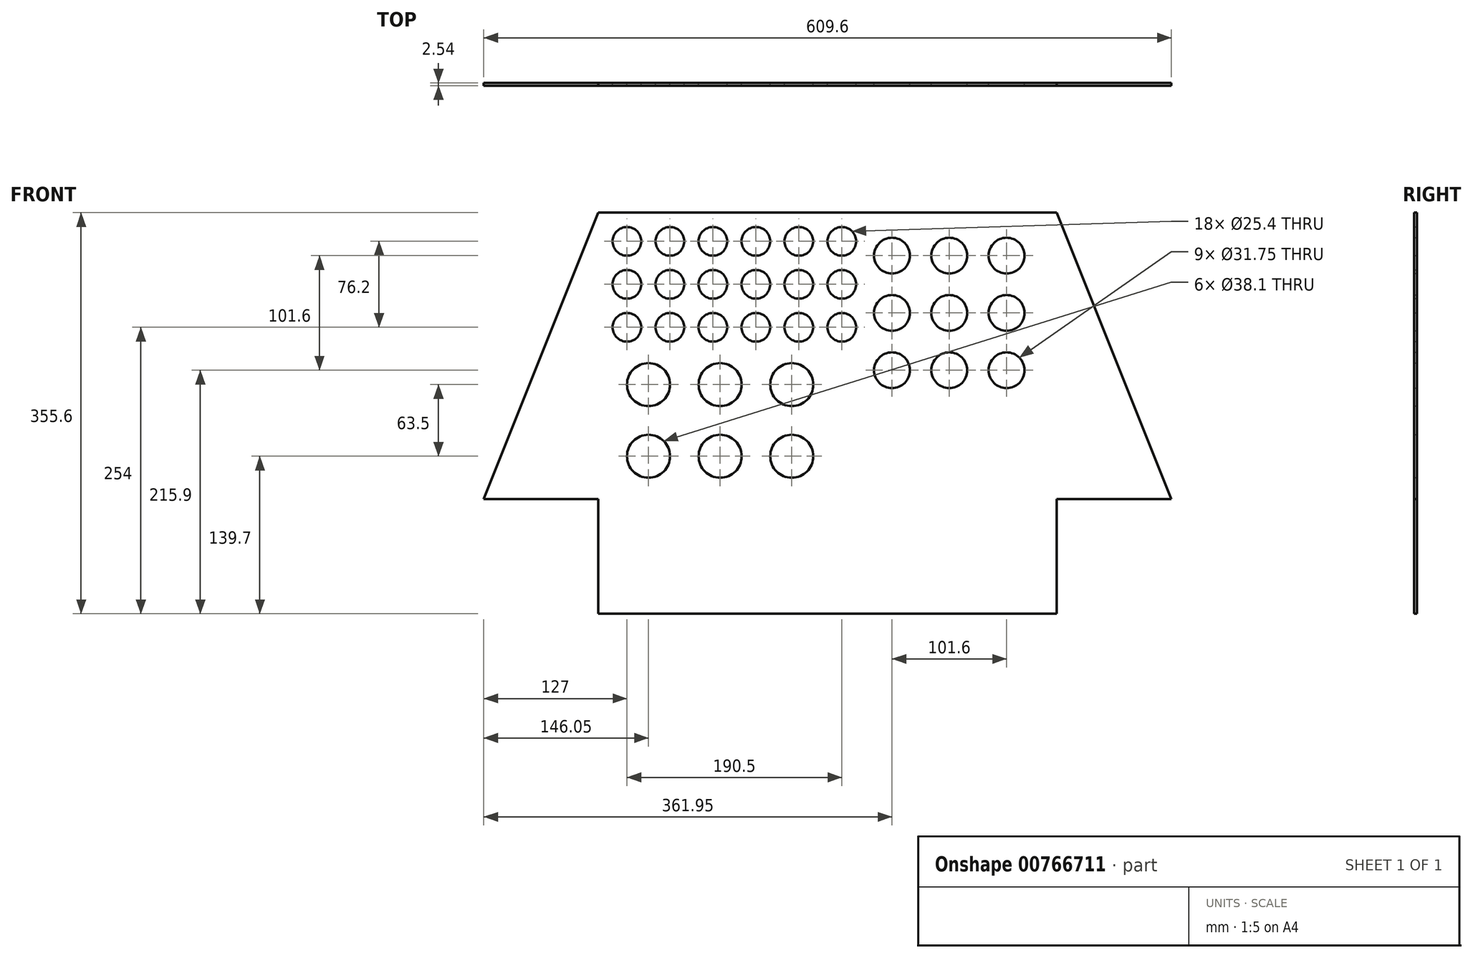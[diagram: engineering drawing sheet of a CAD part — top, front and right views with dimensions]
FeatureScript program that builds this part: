
annotation { "Feature Type Name" : "Feature", "Feature Type Description" : "" }
export const myFeature = defineFeature(function(context is Context, id is Id, definition is map)
    precondition{}
    {
        {
            var Q0;
            Q0=qCreatedBy(makeId("Front.planeOp"),FACE);
            var sketch = newSketch(context, id + "F0", { "sketchPlane" : qUnion([Q0])});
            skLineSegment(sketch, "E0.bottom", {"start": v(-25.4, -127) * mm, "end": v(-152.4, -127) * mm});
            skLineSegment(sketch, "E0.top", {"start": v(203.2, 127) * mm, "end": v(-203.2, 127) * mm});
            skPoint(sketch, "E0.middle", {"position": v(0, 0) * mm});
            skCircle(sketch, "E1", {"center": v(-177.8, 101.6) * mm, "radius": 12.7 * mm});
            skCircle(sketch, "E2.0.1.0", {"center": v(-177.8, 63.5) * mm, "radius": 12.7 * mm});
            skCircle(sketch, "E2.0.2.0", {"center": v(-177.8, 25.4) * mm, "radius": 12.7 * mm});
            skCircle(sketch, "E2.1.0.0", {"center": v(-139.7, 101.6) * mm, "radius": 12.7 * mm});
            skCircle(sketch, "E2.1.1.0", {"center": v(-139.7, 63.5) * mm, "radius": 12.7 * mm});
            skCircle(sketch, "E2.1.2.0", {"center": v(-139.7, 25.4) * mm, "radius": 12.7 * mm});
            skCircle(sketch, "E2.2.0.0", {"center": v(-101.6, 101.6) * mm, "radius": 12.7 * mm});
            skCircle(sketch, "E2.2.1.0", {"center": v(-101.6, 63.5) * mm, "radius": 12.7 * mm});
            skCircle(sketch, "E2.2.2.0", {"center": v(-101.6, 25.4) * mm, "radius": 12.7 * mm});
            skCircle(sketch, "E2.3.0.0", {"center": v(-63.5, 101.6) * mm, "radius": 12.7 * mm});
            skCircle(sketch, "E2.3.1.0", {"center": v(-63.5, 63.5) * mm, "radius": 12.7 * mm});
            skCircle(sketch, "E2.3.2.0", {"center": v(-63.5, 25.4) * mm, "radius": 12.7 * mm});
            skCircle(sketch, "E2.4.0.0", {"center": v(-25.4, 101.6) * mm, "radius": 12.7 * mm});
            skCircle(sketch, "E2.4.1.0", {"center": v(-25.4, 63.5) * mm, "radius": 12.7 * mm});
            skCircle(sketch, "E2.4.2.0", {"center": v(-25.4, 25.4) * mm, "radius": 12.7 * mm});
            skCircle(sketch, "E2.5.0.0", {"center": v(12.7, 101.6) * mm, "radius": 12.7 * mm});
            skCircle(sketch, "E2.5.1.0", {"center": v(12.7, 63.5) * mm, "radius": 12.7 * mm});
            skCircle(sketch, "E2.5.2.0", {"center": v(12.7, 25.4) * mm, "radius": 12.7 * mm});
            skLineSegment(sketch, "E2.direction1", {"start": v(-177.8, 101.6) * mm, "end": v(-139.7, 101.6) * mm, "construction": true});
            skLineSegment(sketch, "E2.direction2", {"start": v(-177.8, 101.6) * mm, "end": v(-177.8, 63.5) * mm, "construction": true});
            skCircle(sketch, "E3", {"center": v(57.15, 88.9) * mm, "radius": 15.88 * mm});
            skCircle(sketch, "E4.0.1.0", {"center": v(57.15, 38.1) * mm, "radius": 15.88 * mm});
            skCircle(sketch, "E4.0.2.0", {"center": v(57.15, -12.7) * mm, "radius": 15.88 * mm});
            skCircle(sketch, "E4.1.0.0", {"center": v(107.95, 88.9) * mm, "radius": 15.88 * mm});
            skCircle(sketch, "E4.1.1.0", {"center": v(107.95, 38.1) * mm, "radius": 15.88 * mm});
            skCircle(sketch, "E4.1.2.0", {"center": v(107.95, -12.7) * mm, "radius": 15.88 * mm});
            skCircle(sketch, "E4.2.0.0", {"center": v(158.75, 88.9) * mm, "radius": 15.88 * mm});
            skCircle(sketch, "E4.2.1.0", {"center": v(158.75, 38.1) * mm, "radius": 15.88 * mm});
            skCircle(sketch, "E4.2.2.0", {"center": v(158.75, -12.7) * mm, "radius": 15.88 * mm});
            skLineSegment(sketch, "E4.direction1", {"start": v(57.15, 88.9) * mm, "end": v(107.95, 88.9) * mm, "construction": true});
            skLineSegment(sketch, "E4.direction2", {"start": v(57.15, 88.9) * mm, "end": v(57.15, 38.1) * mm, "construction": true});
            skCircle(sketch, "E5", {"center": v(-158.75, -25.4) * mm, "radius": 19.05 * mm});
            skCircle(sketch, "E6.0.1.0", {"center": v(-158.75, -88.9) * mm, "radius": 19.05 * mm});
            skCircle(sketch, "E6.1.0.0", {"center": v(-95.25, -25.4) * mm, "radius": 19.05 * mm});
            skCircle(sketch, "E6.1.1.0", {"center": v(-95.25, -88.9) * mm, "radius": 19.05 * mm});
            skCircle(sketch, "E6.2.0.0", {"center": v(-31.75, -25.4) * mm, "radius": 19.05 * mm});
            skCircle(sketch, "E6.2.1.0", {"center": v(-31.75, -88.9) * mm, "radius": 19.05 * mm});
            skLineSegment(sketch, "E6.direction1", {"start": v(-158.75, -25.4) * mm, "end": v(-95.25, -25.4) * mm, "construction": true});
            skLineSegment(sketch, "E6.direction2", {"start": v(-158.75, -25.4) * mm, "end": v(-158.75, -88.9) * mm, "construction": true});
            skLineSegment(sketch, "E7.top", {"start": v(-203.2, -228.6) * mm, "end": v(203.2, -228.6) * mm});
            skLineSegment(sketch, "E7.left", {"start": v(-203.2, -127) * mm, "end": v(-203.2, -228.6) * mm});
            skLineSegment(sketch, "E7.right", {"start": v(203.2, -127) * mm, "end": v(203.2, -228.6) * mm});
            skLineSegment(sketch, "E8", {"start": v(203.2, 127) * mm, "end": v(304.8, -127) * mm});
            skLineSegment(sketch, "E9", {"start": v(-203.2, 127) * mm, "end": v(-304.8, -127) * mm});
            skLineSegment(sketch, "E10", {"start": v(-304.8, -127) * mm, "end": v(-203.2, -127) * mm});
            skLineSegment(sketch, "E11", {"start": v(304.8, -127) * mm, "end": v(203.2, -127) * mm});
            skPoint(sketch, "E12", {"position": v(-152.4, -127) * mm});
            skPoint(sketch, "E13", {"position": v(-25.4, -127) * mm});
            skPoint(sketch, "E14", {"position": v(25.4, -127) * mm});
            skPoint(sketch, "E15", {"position": v(152.4, -127) * mm});
            skPoint(sketch, "E16", {"position": v(-203.2, -101.6) * mm});
            skPoint(sketch, "E17", {"position": v(-203.2, 101.6) * mm});
            skPoint(sketch, "E18", {"position": v(-203.2, 25.4) * mm});
            skPoint(sketch, "E19", {"position": v(-203.2, 0) * mm});
            skPoint(sketch, "E20", {"position": v(-203.2, -25.4) * mm});
            skPoint(sketch, "E21", {"position": v(-203.2, -12.7) * mm});
            skPoint(sketch, "E22", {"position": v(-203.2, 12.7) * mm});
            skLineSegment(sketch, "E23", {"start": v(-203.2, 101.6) * mm, "end": v(-203.2, 12.7) * mm});
            skLineSegment(sketch, "E24", {"start": v(-203.2, -12.7) * mm, "end": v(-203.2, -101.6) * mm});
            skPoint(sketch, "E25", {"position": v(203.2, 101.6) * mm});
            skPoint(sketch, "E26", {"position": v(203.2, 12.7) * mm});
            skPoint(sketch, "E27", {"position": v(203.2, -12.7) * mm});
            skPoint(sketch, "E28", {"position": v(203.2, -101.6) * mm});
            skLineSegment(sketch, "E29.trimOffspring", {"start": v(203.2, 12.7) * mm, "end": v(203.2, 101.6) * mm});
            skLineSegment(sketch, "E30.trimOffspring", {"start": v(25.4, -127) * mm, "end": v(152.4, -127) * mm});
            skSolve(sketch);
        }
        {
            var Q0;
            Q0=makeQuery(id+"F0.imprint","IMPRINT",FACE,{"disambiguationData":[TD([[makeQuery(id+"F0.imprint","IMPRINT",EDGE,{"derivedFrom":sQuery(id+"F0.wireOp",EDGE,"E0.top")}),1.0]])]});
            extrude(context, id + "F1", {"entities" : qUnion([Q0]), "depth" : 2.54 * mm, "offsetDistance" : 25.4 * mm});
        }
    });
